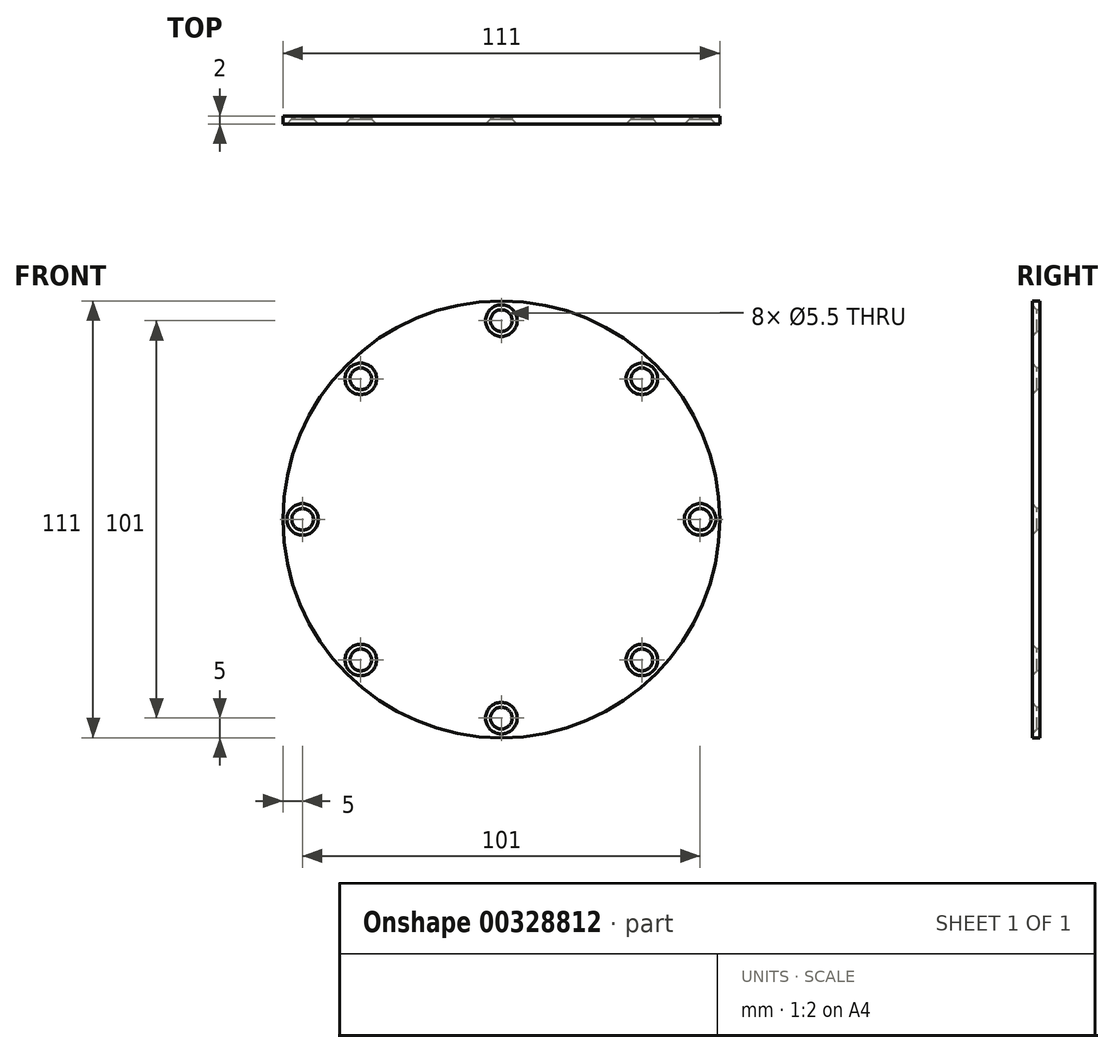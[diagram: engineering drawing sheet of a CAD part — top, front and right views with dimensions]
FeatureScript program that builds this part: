
annotation { "Feature Type Name" : "Feature", "Feature Type Description" : "" }
export const myFeature = defineFeature(function(context is Context, id is Id, definition is map)
    precondition{}
    {
        {
            var Q0;
            Q0=qCreatedBy(makeId("Front.planeOp"),FACE);
            var sketch = newSketch(context, id + "F0", { "sketchPlane" : qUnion([Q0])});
            skCircle(sketch, "E0", {"center": v(0, 0) * mm, "radius": 55.5 * mm});
            skSolve(sketch);
        }
        {
            var Q0;
            Q0 = qSketchRegion(id + "F0", true);
            extrude(context, id + "F1", {"entities" : qUnion([Q0]), "depth" : 2 * mm});
        }
        {
            var Q0;
            Q0=makeQuery(id+"F1.opExtrude","CAP_FACE",FACE,{"disambiguationData":[OSD([sQuery(id+"F0.wireOp",EDGE,"E0")])],"isStart":false});
            var sketch = newSketch(context, id + "F2", { "sketchPlane" : qUnion([Q0])});
            skCircle(sketch, "E1", {"center": v(0, 0) * mm, "radius": 50.5 * mm});
            skLineSegment(sketch, "E2", {"start": v(0, 0) * mm, "end": v(0, 50.5) * mm});
            skLineSegment(sketch, "E3", {"start": v(0, 0) * mm, "end": v(0, -50.5) * mm});
            skLineSegment(sketch, "E4", {"start": v(0, 0) * mm, "end": v(50.5, 0) * mm});
            skLineSegment(sketch, "E5", {"start": v(0, 0) * mm, "end": v(-50.5, 0) * mm});
            skLineSegment(sketch, "E6", {"start": v(0, 0) * mm, "end": v(-35.7, 35.7) * mm});
            skLineSegment(sketch, "E7", {"start": v(0, 0) * mm, "end": v(35.7, 35.7) * mm});
            skLineSegment(sketch, "E8", {"start": v(0, 0) * mm, "end": v(35.7, -35.7) * mm});
            skLineSegment(sketch, "E9", {"start": v(0, 0) * mm, "end": v(-35.7, -35.7) * mm});
            skSolve(sketch);
        }
        {
            var Q0;
            Q0=sQuery(id+"F2.wireOp",VERTEX,"E2.end");
            var Q1;
            Q1=sQuery(id+"F2.wireOp",VERTEX,"E7.end");
            var Q2;
            Q2=sQuery(id+"F2.wireOp",VERTEX,"E4.end");
            var Q3;
            Q3=sQuery(id+"F2.wireOp",VERTEX,"E8.end");
            var Q4;
            Q4=sQuery(id+"F2.wireOp",VERTEX,"E3.end");
            var Q5;
            Q5=sQuery(id+"F2.wireOp",VERTEX,"E9.end");
            var Q6;
            Q6=sQuery(id+"F2.wireOp",VERTEX,"E5.end");
            var Q7;
            Q7=sQuery(id+"F2.wireOp",VERTEX,"E6.end");
            var Q8;
            Q8=makeQuery(id+"F1.opExtrude","SWEPT_BODY",BODY,{"disambiguationData":[OSD([sQuery(id+"F0.wireOp",EDGE,"E0")])]});
            hole(context, id + "F3", {"style" : HoleStyle.C_SINK, "endStyle" : HoleEndStyle.BLIND, "holeDiameter" : 5.5 * mm, "cSinkDiameter" : 8 * mm, "cSinkAngle" : 90 * degree, "holeDepth" : 30 * mm, "tappedDepth" : 27 * mm, "tapClearance" : 3, "startFromSketch" : true, "locations" : qUnion([Q0, Q1, Q2, Q3, Q4, Q5, Q6, Q7]), "scope" : qUnion([Q8])});
        }
    });
